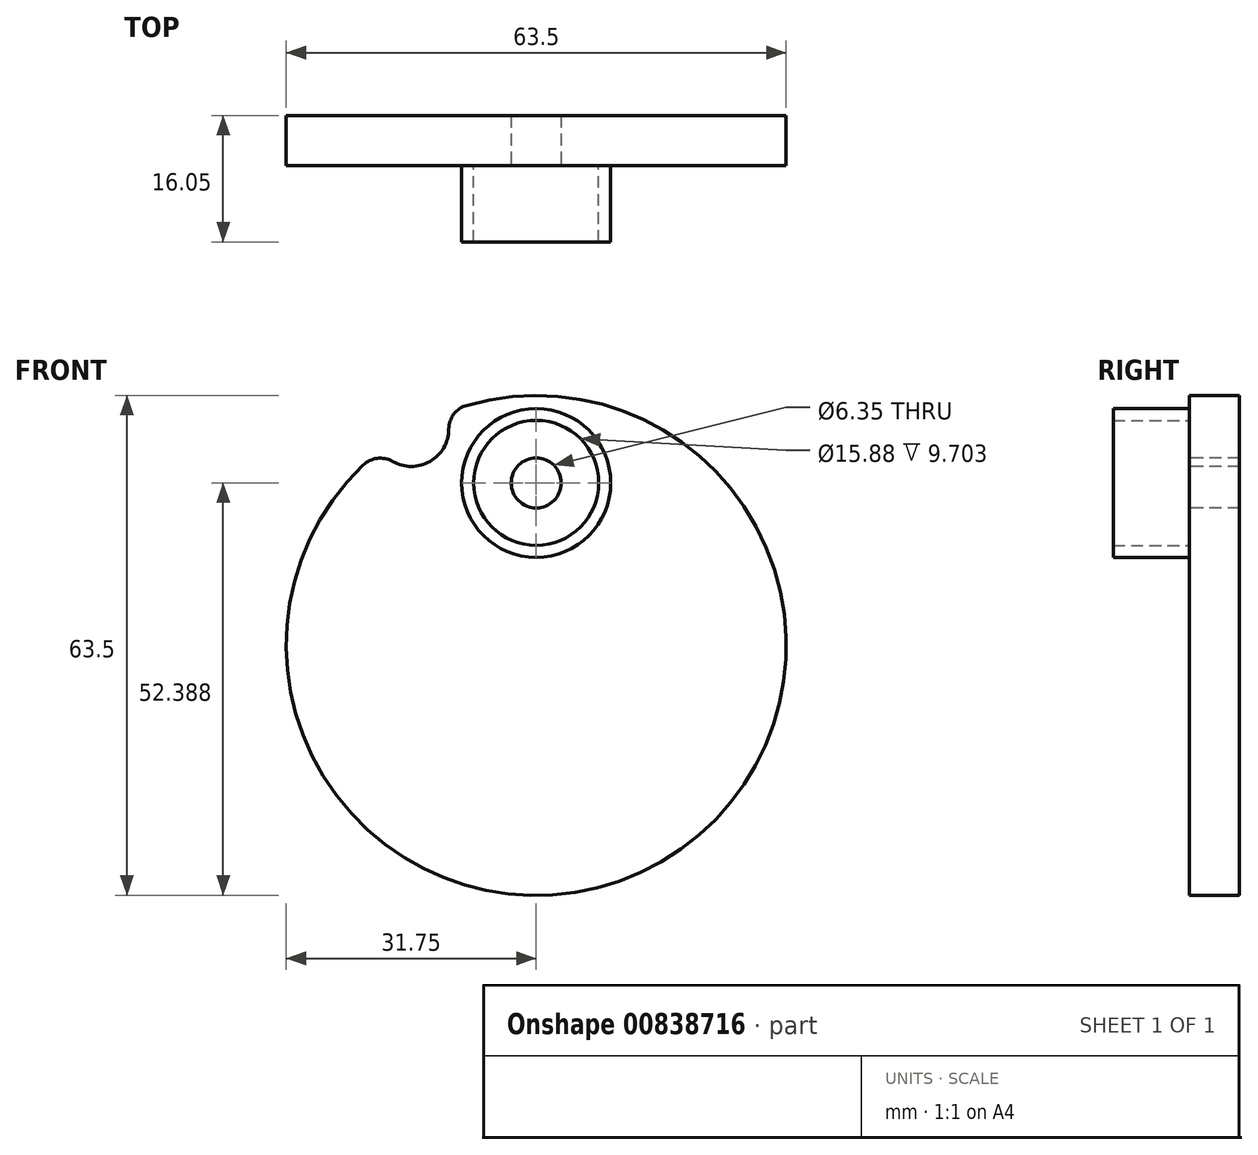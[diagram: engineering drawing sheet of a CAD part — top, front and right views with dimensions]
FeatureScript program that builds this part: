
annotation { "Feature Type Name" : "Feature", "Feature Type Description" : "" }
export const myFeature = defineFeature(function(context is Context, id is Id, definition is map)
    precondition{}
    {
        {
            var Q0;
            Q0=qCreatedBy(makeId("Front.planeOp"),FACE);
            var sketch = newSketch(context, id + "F0", { "sketchPlane" : qUnion([Q0])});
            skCircle(sketch, "E0", {"center": v(0, 0) * mm, "radius": 31.75 * mm});
            skSolve(sketch);
        }
        {
            var Q0;
            Q0 = qSketchRegion(id + "F0", true);
            extrude(context, id + "F1", {"entities" : qUnion([Q0]), "depth" : 6.35 * mm, "offsetDistance" : 25.4 * mm});
        }
        {
            var Q0;
            Q0=makeQuery(id+"F1.opExtrude","CAP_FACE",FACE,{"disambiguationData":[OSD([sQuery(id+"F0.wireOp",EDGE,"E0")])],"isStart":false});
            var sketch = newSketch(context, id + "F2", { "sketchPlane" : qUnion([Q0])});
            skLineSegment(sketch, "E1", {"start": v(-15.88, 27.5) * mm, "end": v(0, 0) * mm, "construction": true});
            skLineSegment(sketch, "E2", {"start": v(0, 0) * mm, "end": v(0, 31.75) * mm, "construction": true});
            skCircle(sketch, "E3", {"center": v(-15.88, 27.5) * mm, "radius": 4.76 * mm});
            skSolve(sketch);
        }
        {
            var Q0;
            Q0 = qSketchRegion(id + "F2", true);
            extrude(context, id + "F3", {"entities" : qUnion([Q0]), "operationType" : NewBodyOperationType.REMOVE, "endBound" : BoundingType.THROUGH_ALL, "oppositeDirection" : true, "depth" : 25.4 * mm, "offsetDistance" : 25.4 * mm});
        }
        {
            var Q0;
            Q0=makeQuery(id+"F3.boolean.opBoolean","INTERSECT",EDGE,{"disambiguationData":[OD(1.0)],"derivedFrom":[makeQuery(id+"F1.opExtrude","SWEPT_FACE",FACE,{"disambiguationData":[OSD([sQuery(id+"F0.wireOp",EDGE,"E0")])]}),makeQuery(id+"F3.opExtrude","SWEPT_FACE",FACE,{"disambiguationData":[OSD([sQuery(id+"F2.wireOp",EDGE,"E3")])]})]});
            var Q1;
            Q1=makeQuery(id+"F3.boolean.opBoolean","INTERSECT",EDGE,{"disambiguationData":[OD(0.0)],"derivedFrom":[makeQuery(id+"F1.opExtrude","SWEPT_FACE",FACE,{"disambiguationData":[OSD([sQuery(id+"F0.wireOp",EDGE,"E0")])]}),makeQuery(id+"F3.opExtrude","SWEPT_FACE",FACE,{"disambiguationData":[OSD([sQuery(id+"F2.wireOp",EDGE,"E3")])]})]});
            fillet(context, id + "F4", {"entities" : qUnion([Q0, Q1]), "radius" : 3.17 * mm, "tangentPropagation" : true, "allowEdgeOverflow" : false});
        }
        {
            var Q0;
            Q0=makeQuery(id+"F1.opExtrude","CAP_FACE",FACE,{"disambiguationData":[OSD([sQuery(id+"F0.wireOp",EDGE,"E0")])],"isStart":false});
            var sketch = newSketch(context, id + "F5", { "sketchPlane" : qUnion([Q0])});
            skCircle(sketch, "E4", {"center": v(0, 20.64) * mm, "radius": 3.18 * mm});
            skSolve(sketch);
        }
        {
            var Q0;
            Q0 = qSketchRegion(id + "F5", true);
            extrude(context, id + "F6", {"entities" : qUnion([Q0]), "operationType" : NewBodyOperationType.REMOVE, "endBound" : BoundingType.THROUGH_ALL, "oppositeDirection" : true, "depth" : 25.4 * mm, "offsetDistance" : 25.4 * mm});
        }
        {
            var Q0;
            Q0=makeQuery(id+"F1.opExtrude","CAP_FACE",FACE,{"disambiguationData":[OSD([sQuery(id+"F0.wireOp",EDGE,"E0")])],"isStart":false});
            var sketch = newSketch(context, id + "F7", { "sketchPlane" : qUnion([Q0])});
            skCircle(sketch, "E5", {"center": v(0, 20.64) * mm, "radius": 9.46 * mm});
            skCircle(sketch, "E6", {"center": v(0, 20.64) * mm, "radius": 7.94 * mm});
            skSolve(sketch);
        }
        {
            var Q0;
            Q0 = qSketchRegion(id + "F7", true);
            extrude(context, id + "F8", {"entities" : qUnion([Q0]), "operationType" : NewBodyOperationType.ADD, "depth" : 9.7 * mm, "offsetDistance" : 25.4 * mm});
        }
    });
